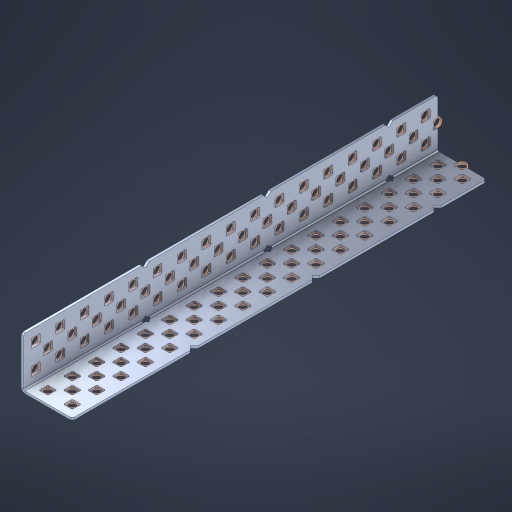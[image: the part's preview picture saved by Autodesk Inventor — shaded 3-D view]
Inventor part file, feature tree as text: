
AUTODESK INVENTOR PART (.ipt)
format: ipt  version: 2023 (Build 270158000, 158)  size: 1,372,160 bytes
history: native  units: in
note: dims shown in document units (in); Inventor stores cm internally (conversion verified against a paired STEP export)
features: other x108, extrude x100, sheet_metal_op x8, sketch x7, pattern_linear x2, mirror x1, chamfer x1
ambient origin geometry x8: Origin, YZ Plane, XZ Plane, XY Plane, X Axis, Y Axis, Z Axis, Center Point
bodies: Solid1 (feature_tree), Body (feature_tree)
feature tree (227):
  sheet_metal_op  "Flanges"
  sheet_metal_op  "Body Pattern"
  pattern_linear  "Center Pattern"  Spacing1=1.0in  [1 undecoded]
  other  "Arc Length"
  pattern_linear  "Notch Pattern"  Spacing1=0.1875in  [1 undecoded]
  other  "Diagonal Plane"
  mirror  "Everything Mirrored"
  chamfer  "End Chamfer"
  sketch  "Sketch1"  dims[d0=1.0in]
  other  "Plate1"
  sketch  "Sketch2"  dims[d1=8.5in]
  other  "Plate2"
  sheet_metal_op  "Bend1"
  sheet_metal_op  "Corner1"
  sketch  "Sketch8"  dims[d2=0.0469in]
  sketch  "Sketch9"  dims[d3=0.0469in]
  other  "Srf91"
  sheet_metal_op  "Body Pattern Sketch"
  other  "Srf92"
  sketch  "Sketch13"  dims[d4=0.0234in]
  sketch  "Sketch15"  dims[d5=0.0938in]
  sketch  "Sketch16"  dims[d6=0.0469in d7=1.0in d8=90.0deg d9=0.0312in d10=0.1875in d11=0.0469in d12=0.0469in d49=0.182in d50=0.02in d52=0.25in d53=0.0469in d54=0.0in d55=0.172in d56=1.0in d57=0.0in d60=6.6929in d62=0.5in d63=0.7874in d65=0.5in d85=0.1473in d86=0.1659in d89=0.0469in d90=0.0in d91=0.04in d92=0.0491in d95=2.5in d96=0.04in d97=0.25in d98=45.0deg d99=0.25in d106=0.182in d107=0.02in d108=0.5in d110=0.0469in d111=0.0in d112=0.172in d113=0.5in d114=0.0in d117=0.5in d123=0.25in d125=0.25in d126=0.0491in d127=0.1227in d128=0.08in d129=0.04in d130=2.5in]
  other  "Srf786"
  other  "Srf856"
  other  "Srf857"
  other  "Srf858"
  other  "Srf859"
  other  "Srf860"
  other  "Srf861"
  other  "Srf889"
  other  "Srf890"
  other  "Srf891"
  other  "Srf1275"
  other  "Srf1276"
  other  "Srf1278"
  other  "Srf1279"
  other  "Srf1280"
  other  "Srf1281"
  other  "Srf1282"
  other  "Srf1283"
  other  "Srf1277"
  other  "Srf1285"
  other  "Srf1286"
  other  "Srf1287"
  other  "Srf1383"
  other  "Srf1384"
  other  "Srf1385"
  other  "Srf1386"
  other  "Srf1387"
  other  "Srf1388"
  other  "Srf1389"
  other  "Srf1390"
  other  "Srf1391"
  other  "Srf1392"
  other  "Srf1393"
  other  "Srf1394"
  other  "Srf1395"
  other  "Srf1396"
  other  "Srf1397"
  other  "Srf1398"
  other  "Srf1399"
  other  "Srf1400"
  other  "Srf1401"
  other  "Srf1402"
  other  "Srf1403"
  other  "Srf1404"
  other  "Srf1405"
  other  "Srf1406"
  other  "Srf1445"
  other  "Srf1446"
  other  "Srf1447"
  other  "Srf1448"
  other  "Srf1449"
  other  "Srf1450"
  other  "Srf1451"
  other  "Srf1452"
  other  "Srf1453"
  other  "Srf1454"
  other  "Srf1455"
  other  "Srf1456"
  other  "Srf1475"
  other  "Srf1476"
  other  "Srf1477"
  other  "Srf1478"
  other  "Srf1479"
  other  "Srf1480"
  other  "Srf1481"
  other  "Srf1482"
  other  "Srf1483"
  other  "Srf1484"
  other  "Srf1485"
  other  "Srf1486"
  other  "Srf1487"
  other  "Srf1488"
  other  "Srf1489"
  other  "Srf1490"
  other  "Srf1491"
  other  "Srf1492"
  other  "Srf1493"
  other  "Srf1494"
  other  "Srf1495"
  other  "Srf1496"
  other  "Srf1497"
  other  "Srf1498"
  other  "Srf1537"
  other  "Srf1538"
  other  "Srf1539"
  other  "Srf1540"
  other  "Srf1541"
  other  "Srf1542"
  other  "Srf1543"
  other  "Srf1544"
  other  "Srf1545"
  other  "Srf1546"
  other  "Srf1547"
  other  "Srf1548"
  other  "Srf1567"
  other  "Srf1568"
  other  "Srf1569"
  other  "Srf1570"
  other  "Srf1571"
  other  "Srf1572"
  sheet_metal_op  "Body Stamp"
  sheet_metal_op  "Body Circle"
  other  "Center Stamp"
  other  "Center Circle"
  sheet_metal_op  "Notch"
  extrude  "ExtrusionSrf92"  Depth=0.0469in
  extrude  "ExtrusionSrf856"  Depth=0.0469in
  extrude  "ExtrusionSrf857"  Depth=0.182in
  extrude  "ExtrusionSrf858"  Depth=0.02in
  extrude  "ExtrusionSrf859"  Depth=0.25in
  extrude  "ExtrusionSrf860"  Depth=0.0469in
  extrude  "ExtrusionSrf861"  TaperAngle=0.0deg  [1 undecoded]
  extrude  "ExtrusionSrf889"  Depth=2.5in
  extrude  "ExtrusionSrf890"  Depth=1.0in TaperAngle=0.0deg
  extrude  "ExtrusionSrf891"  Depth=2.5in
  extrude  "ExtrusionSrf1275"  Depth=0.5in
  extrude  "ExtrusionSrf1276"  Depth=2.5in
  extrude  "ExtrusionSrf1277"  Depth=2.5in
  extrude  "ExtrusionSrf1278"  Depth=0.0469in
  extrude  "ExtrusionSrf1279"  Depth=2.5in TaperAngle=0.0deg
  extrude  "ExtrusionSrf1280"  Depth=2.5in
  extrude  "ExtrusionSrf1281"  Depth=0.25in TaperAngle=45.0deg
  extrude  "ExtrusionSrf1282"  Depth=0.25in
  extrude  "ExtrusionSrf1345"  Depth=0.182in
  extrude  "ExtrusionSrf1346"  Depth=0.02in
  extrude  "ExtrusionSrf1347"  Depth=0.5in
  extrude  "ExtrusionSrf1348"  Depth=0.0469in
  extrude  "ExtrusionSrf1383"  TaperAngle=0.0deg  [1 undecoded]
  extrude  "ExtrusionSrf1384"  Depth=2.5in
  extrude  "ExtrusionSrf1385"  Depth=0.5in TaperAngle=0.0deg
  extrude  "ExtrusionSrf1386"  Depth=0.5in
  extrude  "ExtrusionSrf1387"  Depth=0.25in
  extrude  "ExtrusionSrf1388"  Depth=0.25in
  extrude  "ExtrusionSrf1389"  Depth=2.5in
  extrude  "ExtrusionSrf1390"  Depth=2.5in
  extrude  "ExtrusionSrf1391"  Depth=2.5in
  extrude  "ExtrusionSrf1392"  Depth=2.5in
  extrude  "ExtrusionSrf1393"  Depth=2.5in
  extrude  "ExtrusionSrf1394"  [1 undecoded]
  extrude  "ExtrusionSrf1395"  [1 undecoded]
  extrude  "ExtrusionSrf1396"  [1 undecoded]
  extrude  "ExtrusionSrf1397"  [1 undecoded]
  extrude  "ExtrusionSrf1398"  [1 undecoded]
  extrude  "ExtrusionSrf1399"  [1 undecoded]
  extrude  "ExtrusionSrf1400"  [1 undecoded]
  extrude  "ExtrusionSrf1401"  [1 undecoded]
  extrude  "ExtrusionSrf1402"  [1 undecoded]
  extrude  "ExtrusionSrf1403"  [1 undecoded]
  extrude  "ExtrusionSrf1404"  [1 undecoded]
  extrude  "ExtrusionSrf1405"  [1 undecoded]
  extrude  "ExtrusionSrf1406"  [1 undecoded]
  extrude  "ExtrusionSrf1445"  [1 undecoded]
  extrude  "ExtrusionSrf1446"  [1 undecoded]
  extrude  "ExtrusionSrf1447"  [1 undecoded]
  extrude  "ExtrusionSrf1448"  [1 undecoded]
  extrude  "ExtrusionSrf1449"  [1 undecoded]
  extrude  "ExtrusionSrf1450"  [1 undecoded]
  extrude  "ExtrusionSrf1451"  [1 undecoded]
  extrude  "ExtrusionSrf1452"  [1 undecoded]
  extrude  "ExtrusionSrf1453"  [1 undecoded]
  extrude  "ExtrusionSrf1454"  [1 undecoded]
  extrude  "ExtrusionSrf1455"  [1 undecoded]
  extrude  "ExtrusionSrf1456"  [1 undecoded]
  extrude  "ExtrusionSrf1475"  [1 undecoded]
  extrude  "ExtrusionSrf1476"  [1 undecoded]
  extrude  "ExtrusionSrf1477"  [1 undecoded]
  extrude  "ExtrusionSrf1478"  [1 undecoded]
  extrude  "ExtrusionSrf1479"  [1 undecoded]
  extrude  "ExtrusionSrf1480"  [1 undecoded]
  extrude  "ExtrusionSrf1481"  [1 undecoded]
  extrude  "ExtrusionSrf1482"  [1 undecoded]
  extrude  "ExtrusionSrf1483"  [1 undecoded]
  extrude  "ExtrusionSrf1484"  [1 undecoded]
  extrude  "ExtrusionSrf1485"  [1 undecoded]
  extrude  "ExtrusionSrf1486"  [1 undecoded]
  extrude  "ExtrusionSrf1487"  [1 undecoded]
  extrude  "ExtrusionSrf1488"  [1 undecoded]
  extrude  "ExtrusionSrf1489"  [1 undecoded]
  extrude  "ExtrusionSrf1490"  [1 undecoded]
  extrude  "ExtrusionSrf1491"  [1 undecoded]
  extrude  "ExtrusionSrf1492"  [1 undecoded]
  extrude  "ExtrusionSrf1493"  [1 undecoded]
  extrude  "ExtrusionSrf1494"  [1 undecoded]
  extrude  "ExtrusionSrf1495"  [1 undecoded]
  extrude  "ExtrusionSrf1496"  [1 undecoded]
  extrude  "ExtrusionSrf1497"  [1 undecoded]
  extrude  "ExtrusionSrf1498"  [1 undecoded]
  extrude  "ExtrusionSrf1537"  [1 undecoded]
  extrude  "ExtrusionSrf1538"  [1 undecoded]
  extrude  "ExtrusionSrf1539"  [1 undecoded]
  extrude  "ExtrusionSrf1540"  [1 undecoded]
  extrude  "ExtrusionSrf1541"  [1 undecoded]
  extrude  "ExtrusionSrf1542"  [1 undecoded]
  extrude  "ExtrusionSrf1543"  [1 undecoded]
  extrude  "ExtrusionSrf1544"  [1 undecoded]
  extrude  "ExtrusionSrf1545"  [1 undecoded]
  extrude  "ExtrusionSrf1546"  [1 undecoded]
  extrude  "ExtrusionSrf1547"  [1 undecoded]
  extrude  "ExtrusionSrf1548"  [1 undecoded]
  extrude  "ExtrusionSrf1567"  [1 undecoded]
  extrude  "ExtrusionSrf1568"  [1 undecoded]
  extrude  "ExtrusionSrf1569"  [1 undecoded]
  extrude  "ExtrusionSrf1570"  [1 undecoded]
  extrude  "ExtrusionSrf1571"  [1 undecoded]
  extrude  "ExtrusionSrf1572"  [1 undecoded]
note: 71 required parameter values undecoded (feature->parameter linkage not recoverable at this tier; creation-order binding heuristic only, values carry confidence <= 0.55)
